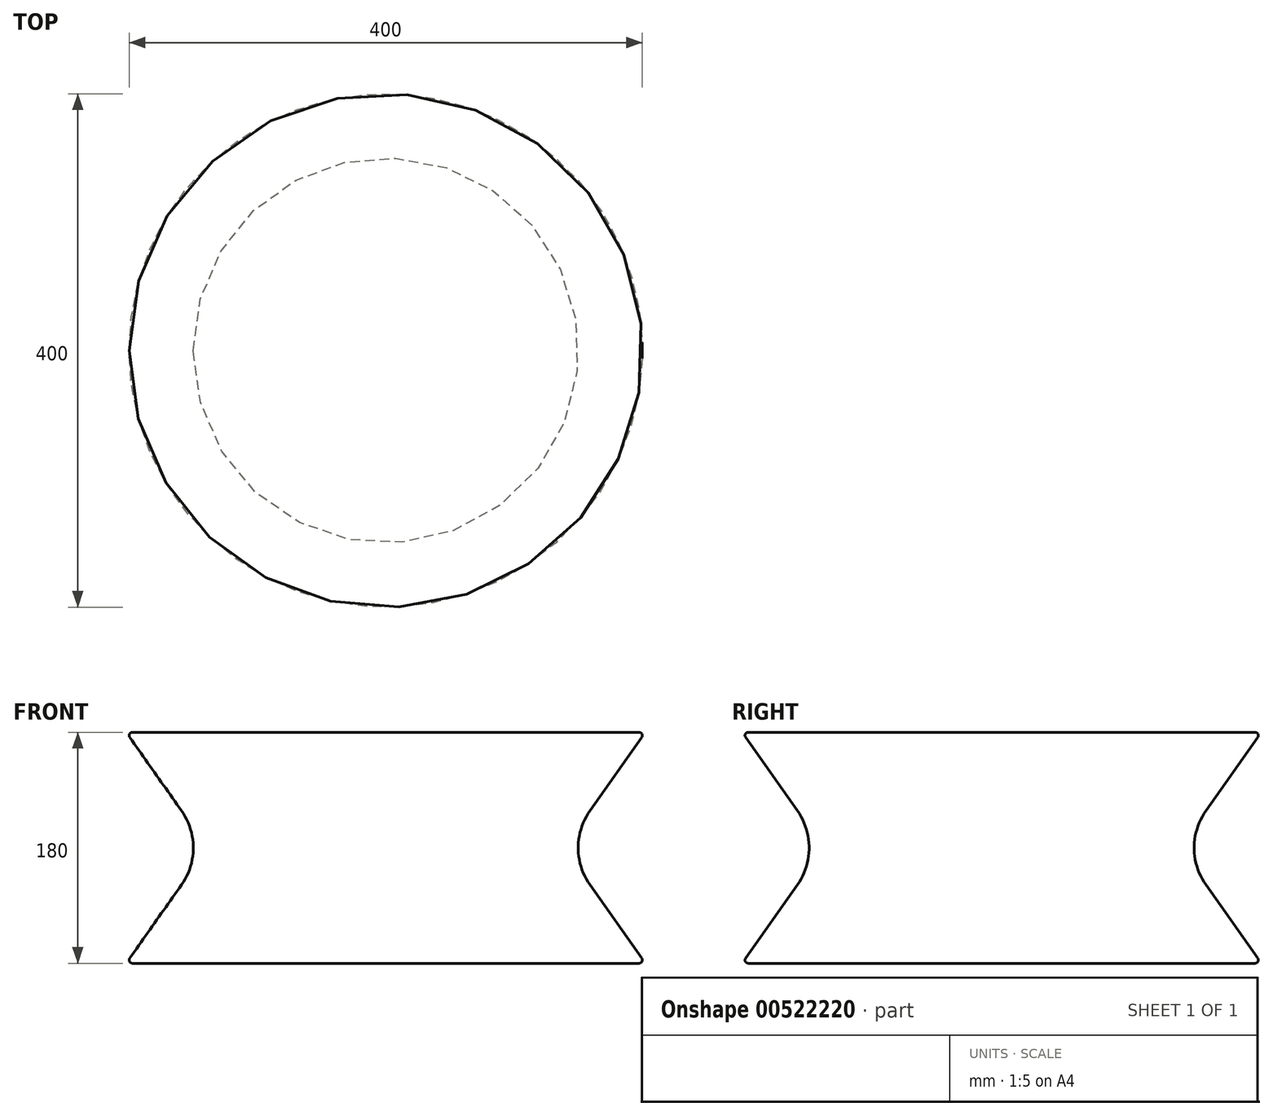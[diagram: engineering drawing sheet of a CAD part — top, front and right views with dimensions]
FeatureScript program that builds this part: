
annotation { "Feature Type Name" : "Feature", "Feature Type Description" : "" }
export const myFeature = defineFeature(function(context is Context, id is Id, definition is map)
    precondition{}
    {
        {
            var Q0;
            Q0=qCreatedBy(makeId("Front.planeOp"),FACE);
            var sketch = newSketch(context, id + "F0", { "sketchPlane" : qUnion([Q0])});
            skArc(sketch, "E0", {"start": v(159.15, 28.83) * mm, "mid": v(152.34, 15.13) * mm, "end": v(150, 0) * mm});
            skArc(sketch, "E1", {"start": v(199.54, 86.06) * mm, "mid": v(199.72, 88.65) * mm, "end": v(197.5, 90) * mm});
            skLineSegment(sketch, "E2", {"start": v(150, 0) * mm, "end": v(0, 0) * mm});
            skLineSegment(sketch, "E3", {"start": v(197.5, 90) * mm, "end": v(0, 90) * mm});
            skLineSegment(sketch, "E4", {"start": v(199.54, 86.06) * mm, "end": v(159.15, 28.83) * mm});
            skLineSegment(sketch, "E5", {"start": v(0, 0) * mm, "end": v(0, 90) * mm});
            skSolve(sketch);
        }
        {
            var Q0;
            Q0=makeQuery(id+"F0.imprint","IMPRINT",FACE,{"disambiguationData":[TD([[makeQuery(id+"F0.imprint","IMPRINT",EDGE,{"derivedFrom":sQuery(id+"F0.wireOp",EDGE,"E0")}),-1.0]])]});
            var Q1;
            Q1=sQuery(id+"F0.wireOp",EDGE,"E5");
            revolve(context, id + "F1", {"entities" : qUnion([Q0]), "axis" : qUnion([Q1]), "revolveType" : RevolveType.FULL});
        }
        {
            var Q0;
            Q0=makeQuery(id+"F1.opRevolve","SWEPT_BODY",BODY,{"disambiguationData":[OSD([sQuery(id+"F0.wireOp",EDGE,"E0"),sQuery(id+"F0.wireOp",EDGE,"E1"),sQuery(id+"F0.wireOp",EDGE,"E2"),sQuery(id+"F0.wireOp",EDGE,"E3"),sQuery(id+"F0.wireOp",EDGE,"E4"),sQuery(id+"F0.wireOp",EDGE,"E5")])]});
            var Q1;
            Q1=makeQuery(id+"F1.opRevolve","SWEPT_FACE",FACE,{"disambiguationData":[OSD([sQuery(id+"F0.wireOp",EDGE,"E2")])]});
            mirror(context, id + "F2", {"operationType" : NewBodyOperationType.ADD, "entities" : qUnion([Q0]), "mirrorPlane" : qUnion([Q1])});
        }
    });
